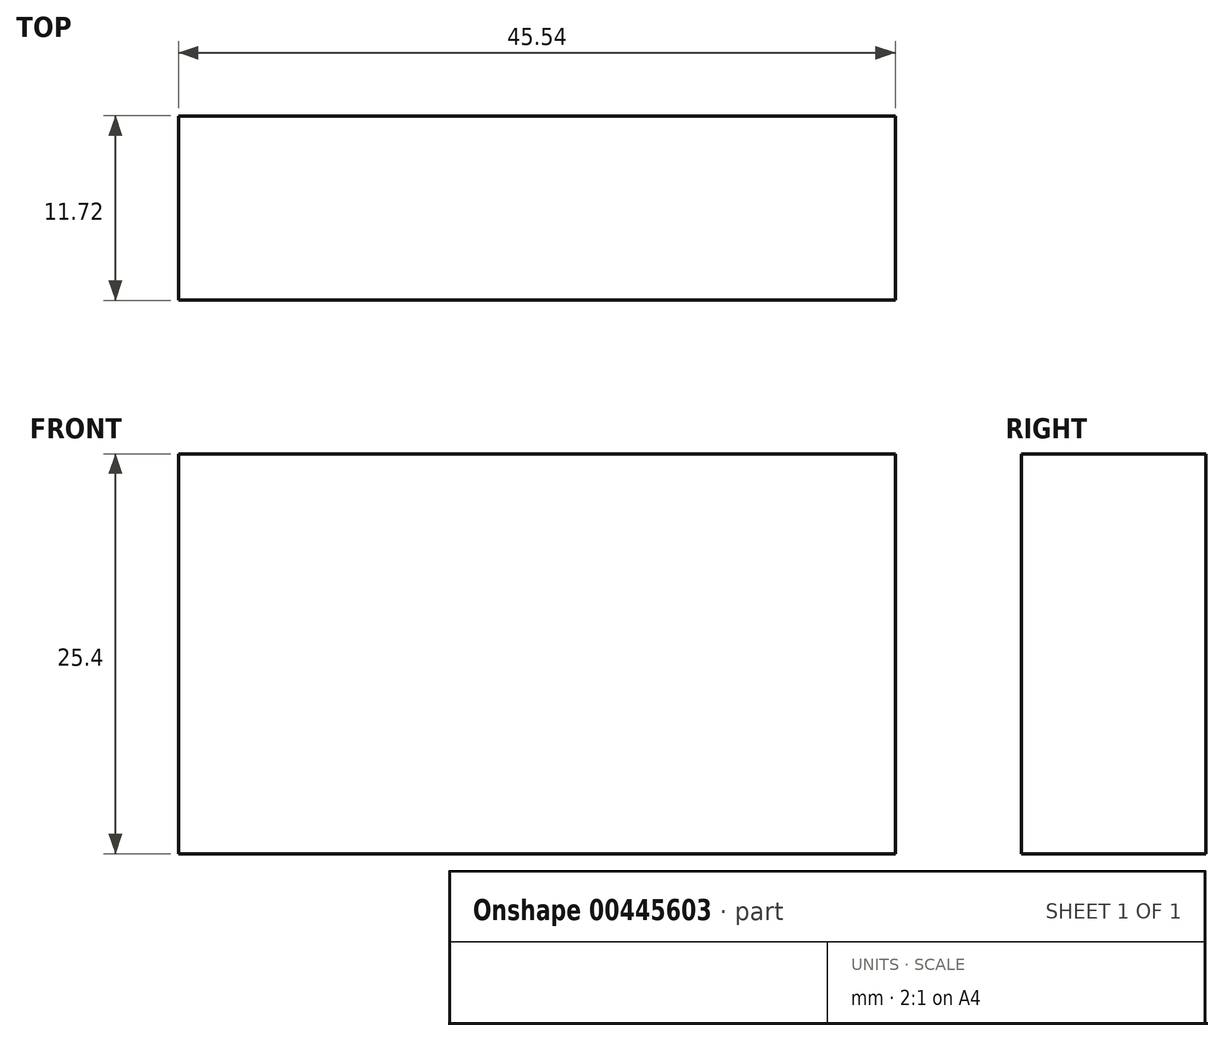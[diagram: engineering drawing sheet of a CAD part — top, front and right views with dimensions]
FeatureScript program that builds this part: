
annotation { "Feature Type Name" : "Feature", "Feature Type Description" : "" }
export const myFeature = defineFeature(function(context is Context, id is Id, definition is map)
    precondition{}
    {
        {
            var Q0;
            Q0=qCreatedBy(makeId("Top.planeOp"),FACE);
            var sketch = newSketch(context, id + "F0", { "sketchPlane" : qUnion([Q0])});
            skLineSegment(sketch, "E0.bottom", {"start": v(-22.77, 5.86) * mm, "end": v(22.77, 5.86) * mm});
            skLineSegment(sketch, "E0.top", {"start": v(-22.77, -5.86) * mm, "end": v(22.77, -5.86) * mm});
            skLineSegment(sketch, "E0.left", {"start": v(-22.77, 5.86) * mm, "end": v(-22.77, -5.86) * mm});
            skLineSegment(sketch, "E0.right", {"start": v(22.77, 5.86) * mm, "end": v(22.77, -5.86) * mm});
            skPoint(sketch, "E0.middle", {"position": v(0, 0) * mm});
            skLineSegment(sketch, "E1.bottom", {"start": v(-22.77, 5.86) * mm, "end": v(-11.83, 5.86) * mm});
            skLineSegment(sketch, "E1.top", {"start": v(-22.77, 30.76) * mm, "end": v(-11.83, 30.76) * mm});
            skLineSegment(sketch, "E1.left", {"start": v(-22.77, 5.86) * mm, "end": v(-22.77, 30.76) * mm});
            skLineSegment(sketch, "E1.right", {"start": v(-11.83, 5.86) * mm, "end": v(-11.83, 30.76) * mm});
            skLineSegment(sketch, "E2.bottom", {"start": v(22.77, 5.86) * mm, "end": v(11.44, 5.86) * mm});
            skLineSegment(sketch, "E2.top", {"start": v(22.77, 30.76) * mm, "end": v(11.44, 30.76) * mm});
            skLineSegment(sketch, "E2.left", {"start": v(22.77, 5.86) * mm, "end": v(22.77, 30.76) * mm});
            skLineSegment(sketch, "E2.right", {"start": v(11.44, 5.86) * mm, "end": v(11.44, 30.76) * mm});
            skSolve(sketch);
        }
        {
            var Q0;
            Q0=makeQuery(id+"F0.imprint","IMPRINT",FACE,{"disambiguationData":[TD([[makeQuery(id+"F0.imprint","IMPRINT",EDGE,{"derivedFrom":sQuery(id+"F0.wireOp",EDGE,"E2.bottom")}),-1.0]])]});
            var Q1;
            Q1=makeQuery(id+"F0.imprint","IMPRINT",FACE,{"disambiguationData":[TD([[makeQuery(id+"F0.imprint","IMPRINT",EDGE,{"derivedFrom":sQuery(id+"F0.wireOp",EDGE,"E0.bottom")}),-1.0]])]});
            var Q2;
            Q2=makeQuery(id+"F0.imprint","IMPRINT",FACE,{"disambiguationData":[TD([[makeQuery(id+"F0.imprint","IMPRINT",EDGE,{"derivedFrom":sQuery(id+"F0.wireOp",EDGE,"E1.bottom")}),1.0]])]});
            extrude(context, id + "F1", {"entities" : qUnion([Q0, Q1, Q2]), "depth" : 25.4 * mm});
        }
    });
